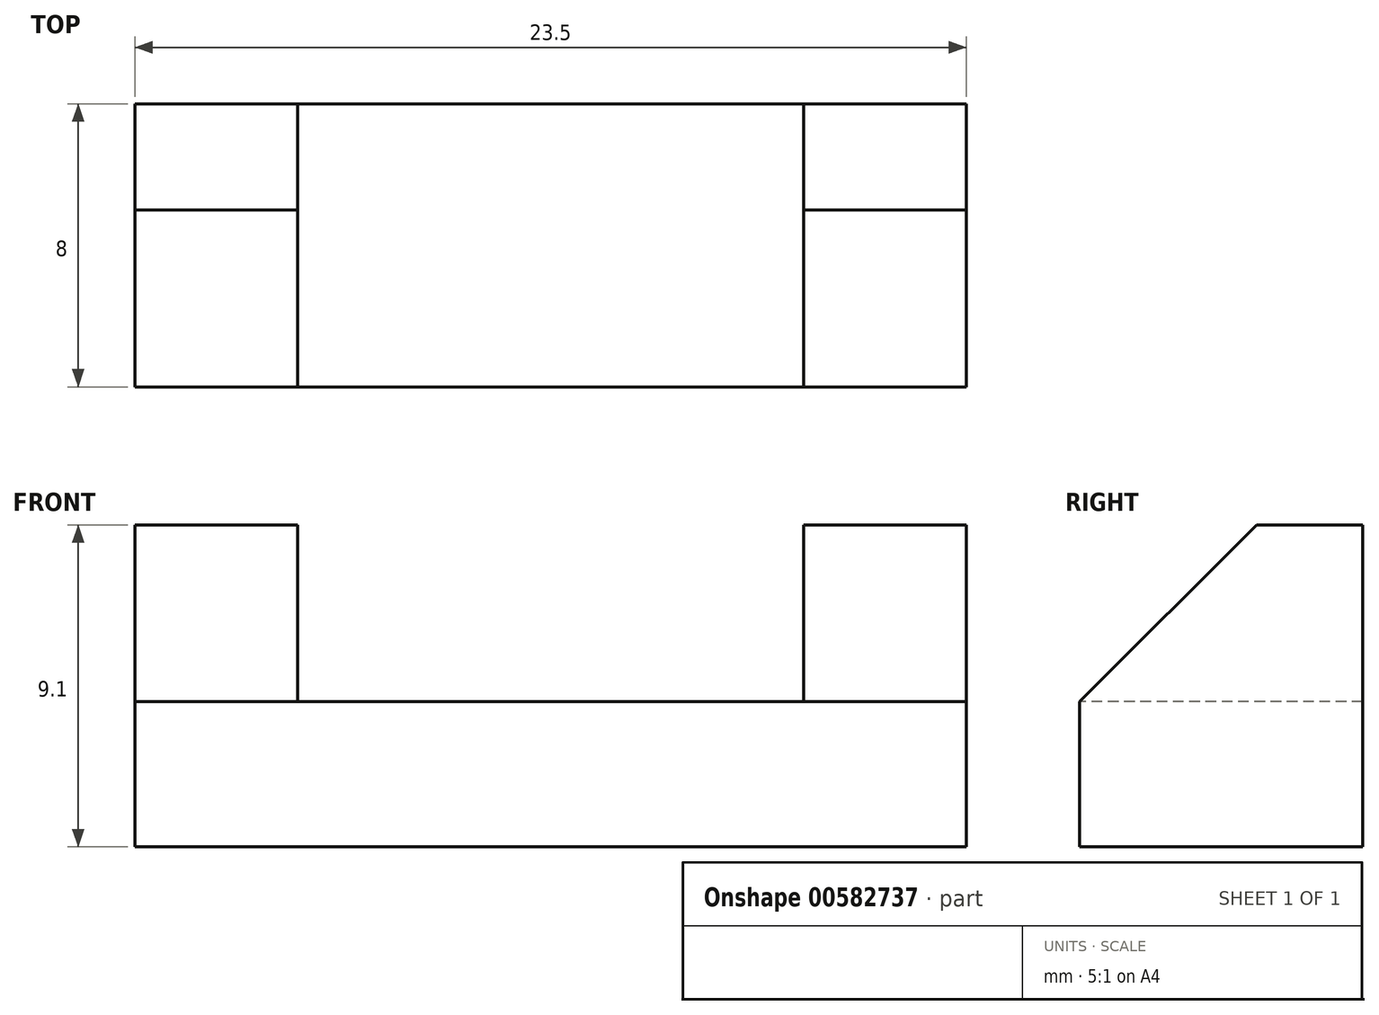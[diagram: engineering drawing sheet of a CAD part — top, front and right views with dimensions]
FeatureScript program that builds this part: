
annotation { "Feature Type Name" : "Feature", "Feature Type Description" : "" }
export const myFeature = defineFeature(function(context is Context, id is Id, definition is map)
    precondition{}
    {
        {
            var Q0;
            Q0=qCreatedBy(makeId("Top.planeOp"),FACE);
            var sketch = newSketch(context, id + "F0", { "sketchPlane" : qUnion([Q0])});
            skLineSegment(sketch, "E0.bottom", {"start": v(11.75, -4) * mm, "end": v(-11.75, -4) * mm});
            skLineSegment(sketch, "E0.top", {"start": v(11.75, 4) * mm, "end": v(-11.75, 4) * mm});
            skLineSegment(sketch, "E0.left", {"start": v(11.75, -4) * mm, "end": v(11.75, 4) * mm});
            skLineSegment(sketch, "E0.right", {"start": v(-11.75, -4) * mm, "end": v(-11.75, 4) * mm});
            skPoint(sketch, "E0.middle", {"position": v(0, 0) * mm});
            skSolve(sketch);
        }
        {
            var Q0;
            Q0=makeQuery(id+"F0.imprint","IMPRINT",FACE,{"disambiguationData":[TD([[makeQuery(id+"F0.imprint","IMPRINT",EDGE,{"derivedFrom":sQuery(id+"F0.wireOp",EDGE,"E0.bottom")}),-1.0]])]});
            extrude(context, id + "F1", {"entities" : qUnion([Q0]), "depth" : 4.1 * mm, "offsetDistance" : 25 * mm});
        }
        {
            var Q0;
            Q0=makeQuery(id+"F1.opExtrude","CAP_FACE",FACE,{"disambiguationData":[OSD([sQuery(id+"F0.wireOp",EDGE,"E0.bottom"),sQuery(id+"F0.wireOp",EDGE,"E0.top"),sQuery(id+"F0.wireOp",EDGE,"E0.left"),sQuery(id+"F0.wireOp",EDGE,"E0.right")])],"isStart":false});
            var sketch = newSketch(context, id + "F2", { "sketchPlane" : qUnion([Q0])});
            skLineSegment(sketch, "E1.0", {"start": v(11.75, 4) * mm, "end": v(-11.75, 4) * mm});
            skLineSegment(sketch, "E2.0", {"start": v(-11.75, -4) * mm, "end": v(-11.75, 4) * mm});
            skLineSegment(sketch, "E3.0", {"start": v(11.75, -4) * mm, "end": v(11.75, 4) * mm});
            skLineSegment(sketch, "E4", {"start": v(-7.15, 4) * mm, "end": v(-7.15, -4) * mm});
            skLineSegment(sketch, "E5", {"start": v(-7.15, -4) * mm, "end": v(-11.75, -4) * mm});
            skLineSegment(sketch, "E6.MirrorCS", {"start": v(7.15, 4) * mm, "end": v(7.15, -4) * mm});
            skLineSegment(sketch, "E7.MirrorCS", {"start": v(7.15, -4) * mm, "end": v(11.75, -4) * mm});
            skSolve(sketch);
        }
        {
            var Q0;
            {var subQ0=sQuery(id+"F2.wireOp",EDGE,"E2.0");Q0=makeQuery(id+"F2.imprint","IMPRINT",FACE,{"disambiguationData":[TD([[makeQuery(id+"F2.imprint","IMPRINT",EDGE,{"derivedFrom":subQ0}),-1.0]])]});}
            var Q1;
            {var subQ0=sQuery(id+"F2.wireOp",EDGE,"E3.0");Q1=makeQuery(id+"F2.imprint","IMPRINT",FACE,{"disambiguationData":[TD([[makeQuery(id+"F2.imprint","IMPRINT",EDGE,{"derivedFrom":subQ0}),1.0]])]});}
            extrude(context, id + "F3", {"entities" : qUnion([Q0, Q1]), "operationType" : NewBodyOperationType.ADD, "depth" : 5 * mm, "offsetDistance" : 25 * mm});
        }
        {
            var Q0;
            Q0=makeQuery(id+"F3.opExtrude","CAP_EDGE",EDGE,{"disambiguationData":[OSD([sQuery(id+"F2.wireOp",EDGE,"E5")])],"isStart":false});
            var Q1;
            Q1=makeQuery(id+"F3.opExtrude","CAP_EDGE",EDGE,{"disambiguationData":[OSD([sQuery(id+"F2.wireOp",EDGE,"E7.MirrorCS")])],"isStart":false});
            chamfer(context, id + "F4", {"entities" : qUnion([Q0, Q1]), "width" : 5 * mm, "tangentPropagation" : true});
        }
    });
